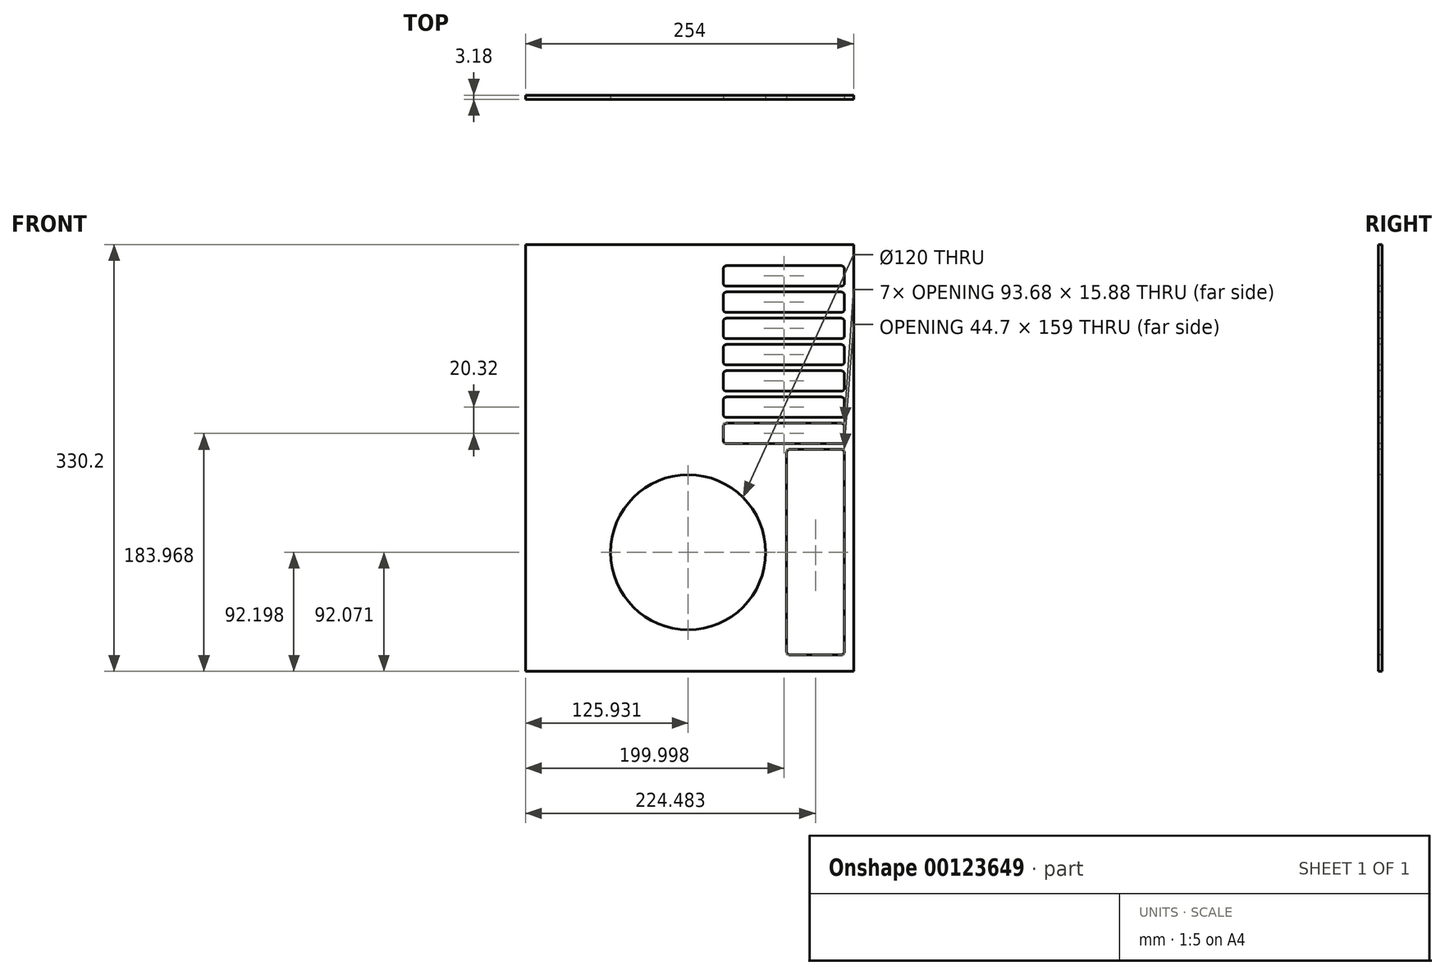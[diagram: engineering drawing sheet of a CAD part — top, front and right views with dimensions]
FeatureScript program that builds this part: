
annotation { "Feature Type Name" : "Feature", "Feature Type Description" : "" }
export const myFeature = defineFeature(function(context is Context, id is Id, definition is map)
    precondition{}
    {
        {
            var Q0;
            Q0=qCreatedBy(makeId("Front.planeOp"),FACE);
            var sketch = newSketch(context, id + "F0", { "sketchPlane" : qUnion([Q0])});
            skLineSegment(sketch, "E0.bottom", {"start": v(-176.04, 205.49) * mm, "end": v(77.96, 205.49) * mm});
            skLineSegment(sketch, "E0.top", {"start": v(-176.04, -124.71) * mm, "end": v(77.96, -124.71) * mm});
            skLineSegment(sketch, "E0.left", {"start": v(-176.04, 205.49) * mm, "end": v(-176.04, -124.71) * mm});
            skLineSegment(sketch, "E0.right", {"start": v(77.96, 205.49) * mm, "end": v(77.96, -124.71) * mm});
            skSolve(sketch);
        }
        {
            var Q0;
            Q0 = qSketchRegion(id + "F0", true);
            extrude(context, id + "F1", {"entities" : qUnion([Q0]), "depth" : 3.17 * mm});
        }
        {
            var Q0;
            Q0=makeQuery(id+"F1.opExtrude","CAP_FACE",FACE,{"disambiguationData":[OSD([sQuery(id+"F0.wireOp",EDGE,"E0.bottom"),sQuery(id+"F0.wireOp",EDGE,"E0.top"),sQuery(id+"F0.wireOp",EDGE,"E0.left"),sQuery(id+"F0.wireOp",EDGE,"E0.right")])],"isStart":false});
            var sketch = newSketch(context, id + "F2", { "sketchPlane" : qUnion([Q0])});
            skLineSegment(sketch, "E1.bottom", {"start": v(28.63, 47) * mm, "end": v(68.26, 47) * mm});
            skLineSegment(sketch, "E1.top", {"start": v(28.63, -112.01) * mm, "end": v(68.26, -112.01) * mm});
            skLineSegment(sketch, "E1.left", {"start": v(26.1, 44.45) * mm, "end": v(26.1, -109.47) * mm});
            skLineSegment(sketch, "E1.right", {"start": v(70.8, 44.45) * mm, "end": v(70.8, -109.47) * mm});
            skLineSegment(sketch, "E2.bottom", {"start": v(-20.34, 87.52) * mm, "end": v(68.26, 87.52) * mm});
            skLineSegment(sketch, "E2.top", {"start": v(-20.34, 71.64) * mm, "end": v(68.26, 71.64) * mm});
            skLineSegment(sketch, "E2.left", {"start": v(-22.88, 84.98) * mm, "end": v(-22.88, 74.18) * mm});
            skLineSegment(sketch, "E2.right", {"start": v(70.8, 84.98) * mm, "end": v(70.8, 74.18) * mm});
            skLineSegment(sketch, "E3.bottom", {"start": v(-20.34, 67.2) * mm, "end": v(68.26, 67.2) * mm});
            skLineSegment(sketch, "E3.top", {"start": v(-20.34, 51.32) * mm, "end": v(68.26, 51.32) * mm});
            skLineSegment(sketch, "E3.left", {"start": v(-22.88, 64.66) * mm, "end": v(-22.88, 53.86) * mm});
            skLineSegment(sketch, "E3.right", {"start": v(70.8, 64.66) * mm, "end": v(70.8, 53.86) * mm});
            skPoint(sketch, "E4.visualSharp", {"position": v(-22.88, 87.52) * mm});
            skArc(sketch, "E4.filletArc", {"start": v(-20.34, 87.52) * mm, "mid": v(-22.14, 86.77) * mm, "end": v(-22.88, 84.98) * mm});
            skPoint(sketch, "E5.visualSharp", {"position": v(70.8, 87.52) * mm});
            skArc(sketch, "E5.filletArc", {"start": v(70.8, 84.98) * mm, "mid": v(70.05, 86.77) * mm, "end": v(68.26, 87.52) * mm});
            skPoint(sketch, "E6.visualSharp", {"position": v(70.8, 71.64) * mm});
            skArc(sketch, "E6.filletArc", {"start": v(68.26, 71.64) * mm, "mid": v(70.05, 72.38) * mm, "end": v(70.8, 74.18) * mm});
            skPoint(sketch, "E7.visualSharp", {"position": v(-22.88, 71.64) * mm});
            skArc(sketch, "E7.filletArc", {"start": v(-22.88, 74.18) * mm, "mid": v(-22.14, 72.38) * mm, "end": v(-20.34, 71.64) * mm});
            skPoint(sketch, "E8.visualSharp", {"position": v(-22.88, 67.2) * mm});
            skArc(sketch, "E8.filletArc", {"start": v(-20.34, 67.2) * mm, "mid": v(-22.14, 66.45) * mm, "end": v(-22.88, 64.66) * mm});
            skPoint(sketch, "E9.visualSharp", {"position": v(-22.88, 51.32) * mm});
            skArc(sketch, "E9.filletArc", {"start": v(-22.88, 53.86) * mm, "mid": v(-22.14, 52.06) * mm, "end": v(-20.34, 51.32) * mm});
            skPoint(sketch, "E10.visualSharp", {"position": v(70.8, 67.2) * mm});
            skArc(sketch, "E10.filletArc", {"start": v(70.8, 64.66) * mm, "mid": v(70.05, 66.45) * mm, "end": v(68.26, 67.2) * mm});
            skPoint(sketch, "E11.visualSharp", {"position": v(70.8, 51.32) * mm});
            skArc(sketch, "E11.filletArc", {"start": v(68.26, 51.32) * mm, "mid": v(70.05, 52.06) * mm, "end": v(70.8, 53.86) * mm});
            skLineSegment(sketch, "E12.bottom", {"start": v(-20.34, 128.16) * mm, "end": v(68.26, 128.16) * mm});
            skLineSegment(sketch, "E12.top", {"start": v(-20.34, 112.28) * mm, "end": v(68.26, 112.28) * mm});
            skLineSegment(sketch, "E12.left", {"start": v(-22.88, 125.62) * mm, "end": v(-22.88, 114.82) * mm});
            skLineSegment(sketch, "E12.right", {"start": v(70.8, 125.62) * mm, "end": v(70.8, 114.82) * mm});
            skLineSegment(sketch, "E13.bottom", {"start": v(-20.34, 107.84) * mm, "end": v(68.26, 107.84) * mm});
            skLineSegment(sketch, "E13.top", {"start": v(-20.34, 91.96) * mm, "end": v(68.26, 91.96) * mm});
            skLineSegment(sketch, "E13.left", {"start": v(-22.88, 105.3) * mm, "end": v(-22.88, 94.5) * mm});
            skLineSegment(sketch, "E13.right", {"start": v(70.8, 105.3) * mm, "end": v(70.8, 94.5) * mm});
            skPoint(sketch, "E14.visualSharp", {"position": v(-22.88, 128.16) * mm});
            skArc(sketch, "E14.filletArc", {"start": v(-20.34, 128.16) * mm, "mid": v(-22.14, 127.41) * mm, "end": v(-22.88, 125.62) * mm});
            skPoint(sketch, "E15.visualSharp", {"position": v(70.8, 128.16) * mm});
            skArc(sketch, "E15.filletArc", {"start": v(70.8, 125.62) * mm, "mid": v(70.05, 127.41) * mm, "end": v(68.26, 128.16) * mm});
            skPoint(sketch, "E16.visualSharp", {"position": v(70.8, 112.28) * mm});
            skArc(sketch, "E16.filletArc", {"start": v(68.26, 112.28) * mm, "mid": v(70.05, 113.02) * mm, "end": v(70.8, 114.82) * mm});
            skPoint(sketch, "E17.visualSharp", {"position": v(-22.88, 112.28) * mm});
            skArc(sketch, "E17.filletArc", {"start": v(-22.88, 114.82) * mm, "mid": v(-22.14, 113.02) * mm, "end": v(-20.34, 112.28) * mm});
            skPoint(sketch, "E18.visualSharp", {"position": v(-22.88, 107.84) * mm});
            skArc(sketch, "E18.filletArc", {"start": v(-20.34, 107.84) * mm, "mid": v(-22.14, 107.1) * mm, "end": v(-22.88, 105.3) * mm});
            skPoint(sketch, "E19.visualSharp", {"position": v(-22.88, 91.96) * mm});
            skArc(sketch, "E19.filletArc", {"start": v(-22.88, 94.5) * mm, "mid": v(-22.14, 92.7) * mm, "end": v(-20.34, 91.96) * mm});
            skPoint(sketch, "E20.visualSharp", {"position": v(70.8, 107.84) * mm});
            skArc(sketch, "E20.filletArc", {"start": v(70.8, 105.3) * mm, "mid": v(70.05, 107.1) * mm, "end": v(68.26, 107.84) * mm});
            skPoint(sketch, "E21.visualSharp", {"position": v(70.8, 91.96) * mm});
            skArc(sketch, "E21.filletArc", {"start": v(68.26, 91.96) * mm, "mid": v(70.05, 92.7) * mm, "end": v(70.8, 94.5) * mm});
            skLineSegment(sketch, "E22.bottom", {"start": v(-20.34, 148.48) * mm, "end": v(68.26, 148.48) * mm});
            skLineSegment(sketch, "E22.top", {"start": v(-20.34, 132.6) * mm, "end": v(68.26, 132.6) * mm});
            skLineSegment(sketch, "E22.left", {"start": v(-22.88, 145.94) * mm, "end": v(-22.88, 135.14) * mm});
            skLineSegment(sketch, "E22.right", {"start": v(70.8, 145.94) * mm, "end": v(70.8, 135.14) * mm});
            skPoint(sketch, "E23.visualSharp", {"position": v(-22.88, 148.48) * mm});
            skArc(sketch, "E23.filletArc", {"start": v(-20.34, 148.48) * mm, "mid": v(-22.14, 147.73) * mm, "end": v(-22.88, 145.94) * mm});
            skPoint(sketch, "E24.visualSharp", {"position": v(70.8, 148.48) * mm});
            skArc(sketch, "E24.filletArc", {"start": v(70.8, 145.94) * mm, "mid": v(70.05, 147.73) * mm, "end": v(68.26, 148.48) * mm});
            skPoint(sketch, "E25.visualSharp", {"position": v(70.8, 132.6) * mm});
            skArc(sketch, "E25.filletArc", {"start": v(68.26, 132.6) * mm, "mid": v(70.05, 133.34) * mm, "end": v(70.8, 135.14) * mm});
            skPoint(sketch, "E26.visualSharp", {"position": v(-22.88, 132.6) * mm});
            skArc(sketch, "E26.filletArc", {"start": v(-22.88, 135.14) * mm, "mid": v(-22.14, 133.34) * mm, "end": v(-20.34, 132.6) * mm});
            skLineSegment(sketch, "E27.bottom", {"start": v(-20.34, 168.8) * mm, "end": v(68.26, 168.8) * mm});
            skLineSegment(sketch, "E27.top", {"start": v(-20.34, 152.92) * mm, "end": v(68.26, 152.92) * mm});
            skLineSegment(sketch, "E27.left", {"start": v(-22.88, 166.26) * mm, "end": v(-22.88, 155.46) * mm});
            skLineSegment(sketch, "E27.right", {"start": v(70.8, 166.26) * mm, "end": v(70.8, 155.46) * mm});
            skPoint(sketch, "E28.visualSharp", {"position": v(-22.88, 168.8) * mm});
            skArc(sketch, "E28.filletArc", {"start": v(-20.34, 168.8) * mm, "mid": v(-22.14, 168.05) * mm, "end": v(-22.88, 166.26) * mm});
            skPoint(sketch, "E29.visualSharp", {"position": v(70.8, 168.8) * mm});
            skArc(sketch, "E29.filletArc", {"start": v(70.8, 166.26) * mm, "mid": v(70.05, 168.05) * mm, "end": v(68.26, 168.8) * mm});
            skPoint(sketch, "E30.visualSharp", {"position": v(70.8, 152.92) * mm});
            skArc(sketch, "E30.filletArc", {"start": v(68.26, 152.92) * mm, "mid": v(70.05, 153.66) * mm, "end": v(70.8, 155.46) * mm});
            skPoint(sketch, "E31.visualSharp", {"position": v(-22.88, 152.92) * mm});
            skArc(sketch, "E31.filletArc", {"start": v(-22.88, 155.46) * mm, "mid": v(-22.14, 153.66) * mm, "end": v(-20.34, 152.92) * mm});
            skLineSegment(sketch, "E32.bottom", {"start": v(-20.34, 189.12) * mm, "end": v(68.26, 189.12) * mm});
            skLineSegment(sketch, "E32.top", {"start": v(-20.34, 173.24) * mm, "end": v(68.26, 173.24) * mm});
            skLineSegment(sketch, "E32.left", {"start": v(-22.88, 186.58) * mm, "end": v(-22.88, 175.78) * mm});
            skLineSegment(sketch, "E32.right", {"start": v(70.8, 186.58) * mm, "end": v(70.8, 175.78) * mm});
            skPoint(sketch, "E33.visualSharp", {"position": v(-22.88, 189.12) * mm});
            skArc(sketch, "E33.filletArc", {"start": v(-20.34, 189.12) * mm, "mid": v(-22.14, 188.37) * mm, "end": v(-22.88, 186.58) * mm});
            skPoint(sketch, "E34.visualSharp", {"position": v(70.8, 189.12) * mm});
            skArc(sketch, "E34.filletArc", {"start": v(70.8, 186.58) * mm, "mid": v(70.05, 188.37) * mm, "end": v(68.26, 189.12) * mm});
            skPoint(sketch, "E35.visualSharp", {"position": v(70.8, 173.24) * mm});
            skArc(sketch, "E35.filletArc", {"start": v(68.26, 173.24) * mm, "mid": v(70.05, 173.98) * mm, "end": v(70.8, 175.78) * mm});
            skPoint(sketch, "E36.visualSharp", {"position": v(-22.88, 173.24) * mm});
            skArc(sketch, "E36.filletArc", {"start": v(-22.88, 175.78) * mm, "mid": v(-22.14, 173.98) * mm, "end": v(-20.34, 173.24) * mm});
            skPoint(sketch, "E37.visualSharp", {"position": v(26.1, 47) * mm});
            skArc(sketch, "E37.filletArc", {"start": v(28.63, 47) * mm, "mid": v(26.84, 46.25) * mm, "end": v(26.1, 44.45) * mm});
            skPoint(sketch, "E38.visualSharp", {"position": v(70.8, 47) * mm});
            skArc(sketch, "E38.filletArc", {"start": v(70.8, 44.45) * mm, "mid": v(70.05, 46.25) * mm, "end": v(68.26, 47) * mm});
            skPoint(sketch, "E39.visualSharp", {"position": v(26.1, -112.01) * mm});
            skArc(sketch, "E39.filletArc", {"start": v(26.1, -109.47) * mm, "mid": v(26.84, -111.27) * mm, "end": v(28.63, -112.01) * mm});
            skPoint(sketch, "E40.visualSharp", {"position": v(70.8, -112.01) * mm});
            skArc(sketch, "E40.filletArc", {"start": v(68.26, -112.01) * mm, "mid": v(70.05, -111.27) * mm, "end": v(70.8, -109.47) * mm});
            skLineSegment(sketch, "E41", {"start": v(68.43, 195.35) * mm, "end": v(68.43, -109.45) * mm});
            skSolve(sketch);
        }
        {
            var Q0;
            Q0 = qSketchRegion(id + "F2", true);
            extrude(context, id + "F3", {"entities" : qUnion([Q0]), "operationType" : NewBodyOperationType.REMOVE, "endBound" : BoundingType.UP_TO_NEXT, "oppositeDirection" : true, "depth" : 25.4 * mm});
        }
        {
            var Q0;
            Q0=makeQuery(id+"F2.imprint","IMPRINT",FACE,{"disambiguationData":[TD([[makeQuery(id+"F2.imprint","IMPRINT",EDGE,{"derivedFrom":sQuery(id+"F2.wireOp",EDGE,"E1.bottom")}),1.0]])]});
            var sketch = newSketch(context, id + "F4", { "sketchPlane" : qUnion([Q0])});
            skCircle(sketch, "E42", {"center": v(-50.1, -32.64) * mm, "radius": 60 * mm});
            skSolve(sketch);
        }
        {
            var Q0;
            Q0 = qSketchRegion(id + "F4", true);
            extrude(context, id + "F5", {"entities" : qUnion([Q0]), "operationType" : NewBodyOperationType.REMOVE, "endBound" : BoundingType.UP_TO_NEXT, "oppositeDirection" : true, "depth" : 25.4 * mm});
        }
    });
